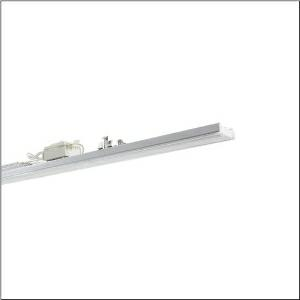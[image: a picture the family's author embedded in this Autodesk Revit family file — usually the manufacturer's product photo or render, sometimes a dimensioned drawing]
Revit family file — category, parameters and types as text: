
# Revit family: licross_21_recessed_mo_52tl18dv46xg
name_source: partatom
category: Lighting Fixtures
units: mm (PartAtom-declared; Revit-internal decimal feet)

## family parameters
Cut with Voids When Loaded = No
Host = Face
Light Source = No
Part Type = Normal
Room Calculation Point = No
Round Connector Dimension = Use Diameter
Shared = No

## types (1)
- --- (1 x LED, 6200 lm, 34.5 W, 4000K)
    Apparent Load = 35 VA
    CIE Flux Codes = 79 95 99 100 100
    Color Rendering = 80
    Color Temperature = 4000K
    Default Elevation = 1800 mm
    Description = Licross 21 Recessed MO, luminaire insert, of sheet steel, galvanised, coil coated, white, length: 2.250mm, width: 66mm, height: 67mm, LED rated luminous flux: 6.200lm, light colour: 840, SDCM (Standard Deviation of Colour Matching)MacAdam ≤ 3 SDCM (initial), control gear: DALI 2, with plug, 5-pole, with phase selection, mains connection: 220..240V, AC, 50/60Hz, rated input power: 35W, internal wiring halogen-free, primary light control with lens, of plastic, primary optical cover: cover, of PMMA, light emission: direct distribution, primary light characteristic: symmetric, protection rating (complete): IP40, insulation class (complete): insulation class I (protective earthing), certification: CE, ENEC, VDE, UKCA, protection symbol: D if used in an environment without relevant dust loads with corresponding accessories, impact resistance: IK06, permissible ambient temperature for indoor applications: -25..+45°C, corresponds to IFS (International Featured Standards) requirements for safety and quality in the food industry, reducing of maximum allowable ambient temperature of 5°C with ceiling mounting, LABS conformity tested according to VDMA 24364:2018-05, The light source and the operating device comply with the requirements of the Ecodesign Regulation (EU) 2019/2020 and are replaceable in accordance with this regulation, packaging unit: 1 piece
    Height = 58 mm
    Lamp = 1 x LED
    Lamp Light Flux = 6200 lm
    Lamp Power = 34.5 W
    Lamp count = 1
    Length = 2250 mm
    Luminous efficacy = 180 lm/W
    Manufacturer = Siteco
    ModVariant = No
    Model = 52TL18DV46XG
    Mounting Place = Ceiling
    Mounting Type = Pendant
    Number of Poles = 1
    OnlyDefault = Yes
    Power Factor = 1
    Product Name = Licross 21 Recessed MO
    Product group = luminaire insert | ceiling pendant
    ProductGroupID = 901
    Protection Class = Protection class I
    Protection Degree = IP 40
    RLX_Detail_Level = 1
    RLX_Emergency_Light_Flux = 0 lm
    RLX_Emergency_Type = 0
    RLX_Emergency_Type_DB = No
    RlxData = <blob elided: 29089 chars, md5=f505334f>
    Socket = socket
    Standby Power = 0 W
    System Light Flux = 6200 lm
    System Power = 35 W
    Type Comments = factory setting: luminous flux: 100 % | dim-lin: 254 | 154 mA
    Type Image = l_1296930.jpg
    URL = http://relux.com
    VarID = @adj_049153
    Voltage = 0 V
    Weight = 0.00 kg
    Width = 66 mm

## geometry (parser evidence)
native form markers: Blend x4, Sweep x10
no freeform markers — native parametric forms only
